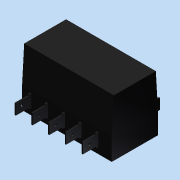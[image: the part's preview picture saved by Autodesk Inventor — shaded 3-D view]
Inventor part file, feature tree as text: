
AUTODESK INVENTOR PART (.ipt)
format: ipt  version: 2012 (Build 160160000, 160)  size: 199,168 bytes
history: native  units: in
note: dims shown in document units (in); Inventor stores cm internally (conversion verified against a paired STEP export)
features: sketch x5, extrude x3, mirror x1, plane x1, loft x1
ambient origin geometry x8: Origin, YZ Plane, XZ Plane, XY Plane, X Axis, Y Axis, Z Axis, Center Point
bodies: Solid1 (feature_tree)
feature tree (11):
  extrude  "Extrusion1"  Depth=1.1in
  extrude  "Extrusion2"  Depth=0.03in
  extrude  "Extrusion3"  Depth=0.05in
  mirror  "Mirror1"
  sketch  "Sketch5"  dims[d7=0.19in d8=1.9685in d10=0.4in d11=0.3937in d13=1.0in]
  plane  "Work Plane1"
  loft  "Loft1"
  sketch  "Sketch2"  dims[d0=2.14in d1=1.1in]
  sketch  "Sketch3"  dims[d2=0.51in d3=0.0in d4=0.03in]
  sketch  "Sketch4"  dims[d5=0.31in d6=0.05in]
  sketch  "Sketch6"  dims[d15=0.37in d16=0.0in d17=0.25in d18=0.06in d19=0.06in d20=0.37in d21=0.0in d22=0.84in d23=1.0in d24=0.0in d25=90.0deg d26=0.0in d27=90.0deg]
